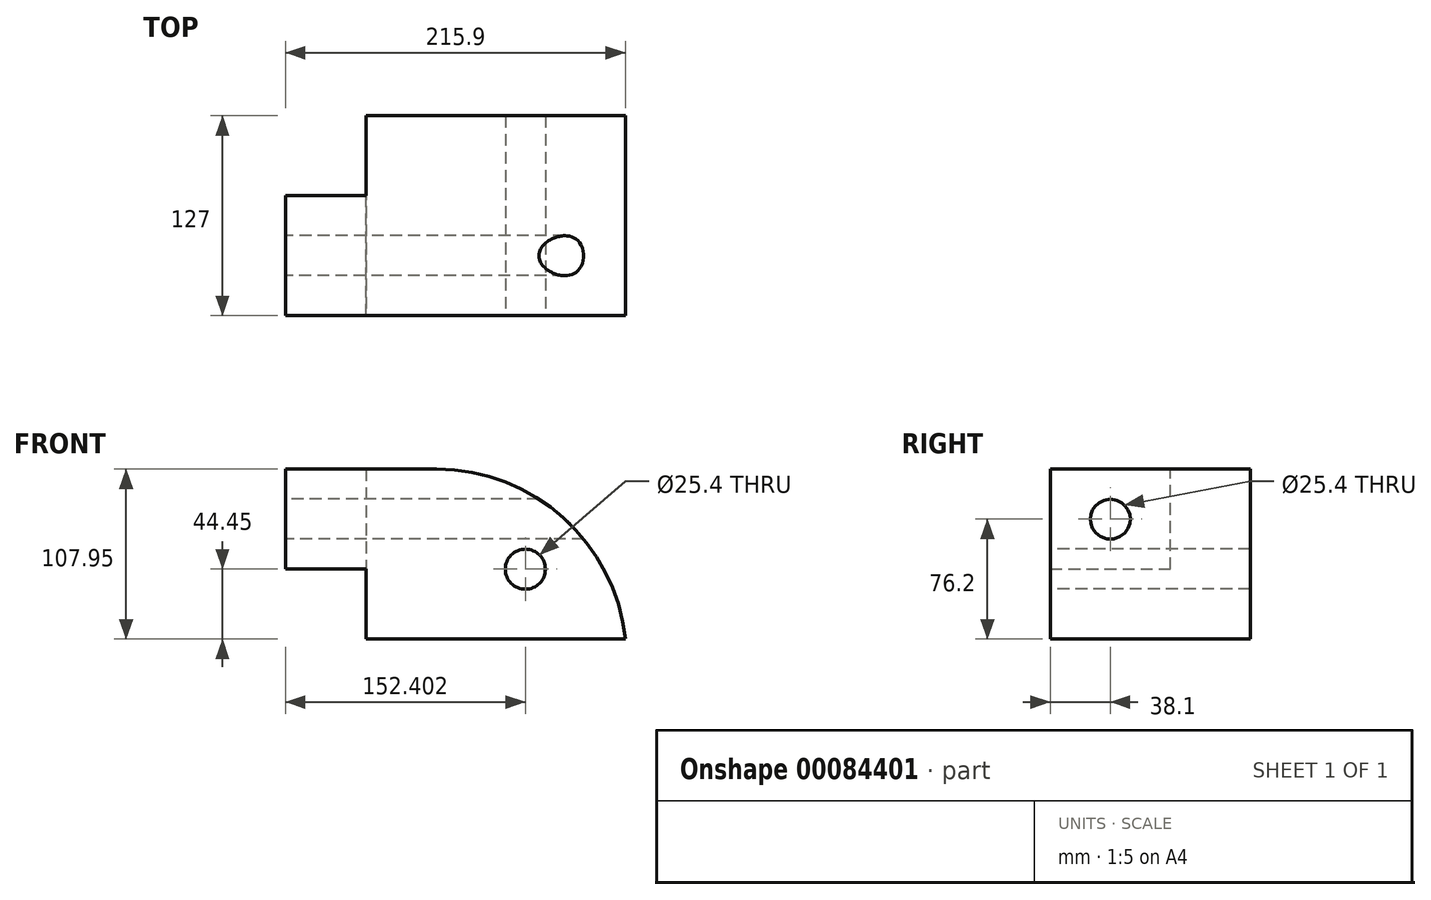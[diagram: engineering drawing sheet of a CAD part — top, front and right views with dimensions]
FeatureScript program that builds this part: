
annotation { "Feature Type Name" : "Feature", "Feature Type Description" : "" }
export const myFeature = defineFeature(function(context is Context, id is Id, definition is map)
    precondition{}
    {
        {
            var Q0;
            Q0=qCreatedBy(makeId("Top.planeOp"),FACE);
            var sketch = newSketch(context, id + "F0", { "sketchPlane" : qUnion([Q0])});
            skLineSegment(sketch, "E0.bottom", {"start": v(-134.08, 69.79) * mm, "end": v(81.82, 69.79) * mm});
            skLineSegment(sketch, "E0.top", {"start": v(-134.08, -57.21) * mm, "end": v(81.82, -57.21) * mm});
            skLineSegment(sketch, "E0.left", {"start": v(-134.08, 69.79) * mm, "end": v(-134.08, -57.21) * mm});
            skLineSegment(sketch, "E0.right", {"start": v(81.82, 69.79) * mm, "end": v(81.82, -57.21) * mm});
            skSolve(sketch);
        }
        {
            var Q0;
            Q0=makeQuery(id+"F0.imprint","IMPRINT",FACE,{"disambiguationData":[TD([[makeQuery(id+"F0.imprint","IMPRINT",EDGE,{"derivedFrom":sQuery(id+"F0.wireOp",EDGE,"E0.bottom")}),-1.0]])]});
            extrude(context, id + "F1", {"entities" : qUnion([Q0]), "depth" : 107.95 * mm});
        }
        {
            var Q0;
            Q0=makeQuery(id+"F1.opExtrude","SWEPT_FACE",FACE,{"disambiguationData":[OSD([sQuery(id+"F0.wireOp",EDGE,"E0.left")])]});
            var sketch = newSketch(context, id + "F2", { "sketchPlane" : qUnion([Q0])});
            skLineSegment(sketch, "E1.bottom", {"start": v(57.21, 107.95) * mm, "end": v(-18.99, 107.95) * mm});
            skLineSegment(sketch, "E1.top", {"start": v(57.21, 44.45) * mm, "end": v(-18.99, 44.45) * mm});
            skLineSegment(sketch, "E1.left", {"start": v(57.21, 107.95) * mm, "end": v(57.21, 44.45) * mm});
            skLineSegment(sketch, "E1.right", {"start": v(-18.99, 107.95) * mm, "end": v(-18.99, 44.45) * mm});
            skSolve(sketch);
        }
        {
            var Q0;
            Q0=makeQuery(id+"F2.imprint","IMPRINT",FACE,{"disambiguationData":[TD([[makeQuery(id+"F2.imprint","IMPRINT",EDGE,{"derivedFrom":sQuery(id+"F2.wireOp",EDGE,"E1.bottom")}),-1.0]])]});
            var sketch = newSketch(context, id + "F3", { "sketchPlane" : qUnion([Q0])});
            skCircle(sketch, "E2", {"center": v(19.11, 76.2) * mm, "radius": 12.7 * mm});
            skSolve(sketch);
        }
        {
            var Q0;
            Q0=makeQuery(id+"F1.opExtrude","CAP_FACE",FACE,{"disambiguationData":[OSD([sQuery(id+"F0.wireOp",EDGE,"E0.bottom"),sQuery(id+"F0.wireOp",EDGE,"E0.top"),sQuery(id+"F0.wireOp",EDGE,"E0.left"),sQuery(id+"F0.wireOp",EDGE,"E0.right")])],"isStart":false});
            var sketch = newSketch(context, id + "F4", { "sketchPlane" : qUnion([Q0])});
            skLineSegment(sketch, "E3.bottom", {"start": v(-134.08, 69.79) * mm, "end": v(-83.28, 69.79) * mm});
            skLineSegment(sketch, "E3.top", {"start": v(-134.08, 18.99) * mm, "end": v(-83.28, 18.99) * mm});
            skLineSegment(sketch, "E3.left", {"start": v(-134.08, 69.79) * mm, "end": v(-134.08, 18.99) * mm});
            skLineSegment(sketch, "E3.right", {"start": v(-83.28, 69.79) * mm, "end": v(-83.28, 18.99) * mm});
            skSolve(sketch);
        }
        {
            var Q0;
            Q0=makeQuery(id+"F4.imprint","IMPRINT",FACE,{"disambiguationData":[TD([[makeQuery(id+"F4.imprint","IMPRINT",EDGE,{"derivedFrom":sQuery(id+"F4.wireOp",EDGE,"E3.bottom")}),-1.0]])]});
            extrude(context, id + "F5", {"entities" : qUnion([Q0]), "operationType" : NewBodyOperationType.REMOVE, "oppositeDirection" : true, "depth" : 107.95 * mm});
        }
        {
            var Q0;
            {var subQ3=sQuery(id+"F2.wireOp",EDGE,"E1.top");Q0=makeQuery(id+"F2.imprint","IMPRINT",FACE,{"disambiguationData":[TD([[makeQuery(id+"F2.imprint","IMPRINT",EDGE,{"derivedFrom":subQ3}),1.0]])]});}
            extrude(context, id + "F6", {"entities" : qUnion([Q0]), "operationType" : NewBodyOperationType.REMOVE, "oppositeDirection" : true, "depth" : 51.2 * mm});
        }
        {
            var Q0;
            Q0=makeQuery(id+"F1.opExtrude","CAP_EDGE",EDGE,{"disambiguationData":[OSD([sQuery(id+"F0.wireOp",EDGE,"E0.right")])],"isStart":false});
            fillet(context, id + "F7", {"entities" : qUnion([Q0]), "radius" : 120.65 * mm, "tangentPropagation" : true, "allowEdgeOverflow" : false});
        }
        {
            var Q0;
            Q0=makeQuery(id+"F1.opExtrude","SWEPT_FACE",FACE,{"disambiguationData":[OSD([sQuery(id+"F0.wireOp",EDGE,"E0.top")])]});
            var sketch = newSketch(context, id + "F8", { "sketchPlane" : qUnion([Q0])});
            skCircle(sketch, "E4", {"center": v(18.32, 44.45) * mm, "radius": 12.7 * mm});
            skSolve(sketch);
        }
        {
            var Q0;
            Q0=sQuery(id+"F8.wireOp",VERTEX,"E4.center");
            var Q1;
            Q1=makeQuery(id+"F1.opExtrude","SWEPT_BODY",BODY,{"disambiguationData":[OSD([sQuery(id+"F0.wireOp",EDGE,"E0.bottom"),sQuery(id+"F0.wireOp",EDGE,"E0.top"),sQuery(id+"F0.wireOp",EDGE,"E0.left"),sQuery(id+"F0.wireOp",EDGE,"E0.right")])]});
            hole(context, id + "F9", {"style" : HoleStyle.SIMPLE, "endStyle" : HoleEndStyle.THROUGH, "holeDiameter" : 25.4 * mm, "locations" : qUnion([Q0]), "scope" : qUnion([Q1]), "isTappedThrough" : true});
        }
        {
            var Q0;
            Q0=sQuery(id+"F3.wireOp",VERTEX,"E2.center");
            var Q1;
            Q1=makeQuery(id+"F1.opExtrude","SWEPT_BODY",BODY,{"disambiguationData":[OSD([sQuery(id+"F0.wireOp",EDGE,"E0.bottom"),sQuery(id+"F0.wireOp",EDGE,"E0.top"),sQuery(id+"F0.wireOp",EDGE,"E0.left"),sQuery(id+"F0.wireOp",EDGE,"E0.right")])]});
            hole(context, id + "F10", {"style" : HoleStyle.SIMPLE, "endStyle" : HoleEndStyle.THROUGH, "holeDiameter" : 25.4 * mm, "locations" : qUnion([Q0]), "scope" : qUnion([Q1]), "isTappedThrough" : true});
        }
    });
